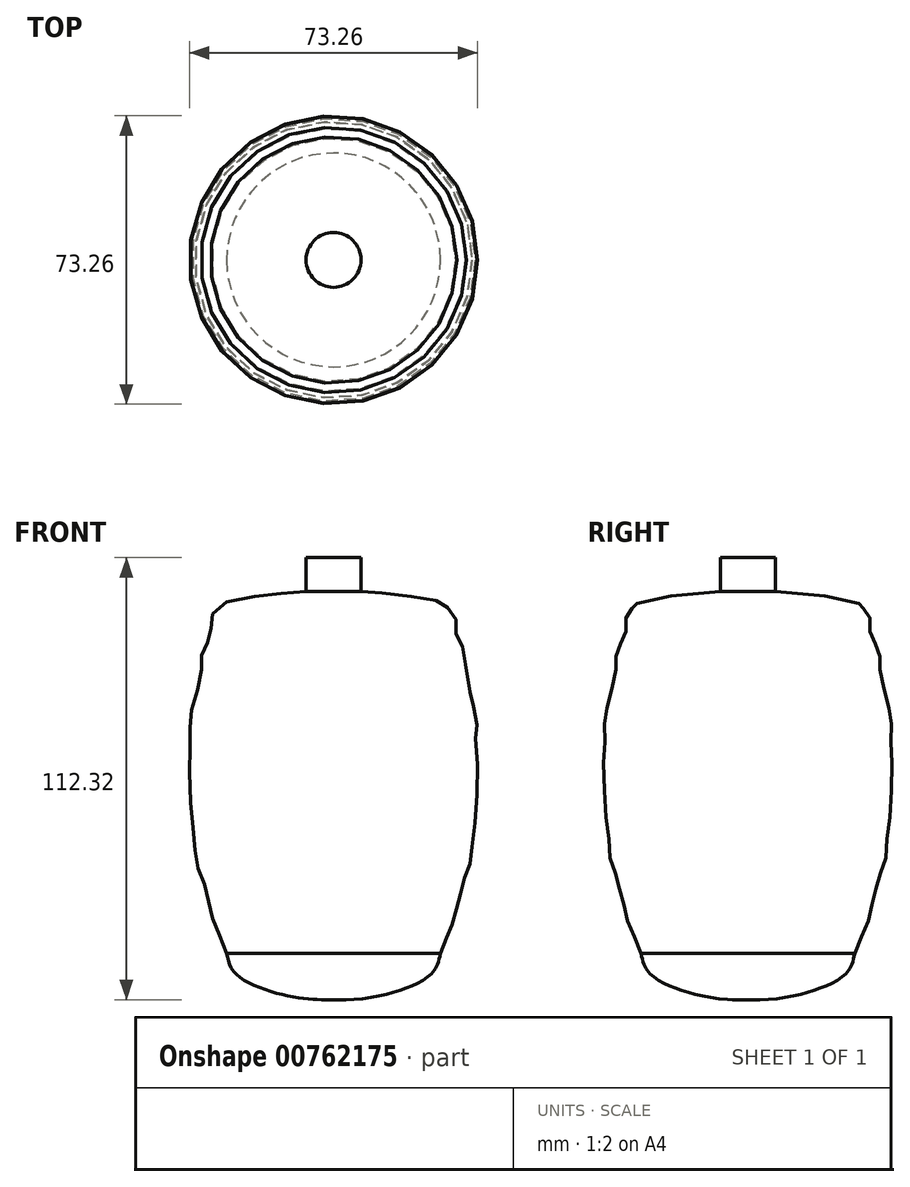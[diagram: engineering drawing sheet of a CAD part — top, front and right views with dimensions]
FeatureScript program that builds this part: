
annotation { "Feature Type Name" : "Feature", "Feature Type Description" : "" }
export const myFeature = defineFeature(function(context is Context, id is Id, definition is map)
    precondition{}
    {
        {
            var Q0;
            Q0=qCreatedBy(makeId("Front.planeOp"),FACE);
            var sketch = newSketch(context, id + "F0", { "sketchPlane" : qUnion([Q0])});
            skFitSpline(sketch, "E0", {"points": [v(-27.15, -40.38) * mm, v(-28.33, -37.93) * mm, v(-29.24, -34.76) * mm, v(-30, -33.44) * mm, v(-31.2, -29.96) * mm, v(-31.35, -28.56) * mm, v(-32.13, -25.81) * mm, v(-32.75, -23.24) * mm, v(-33.52, -20.4) * mm, v(-34.36, -18.84) * mm, v(-35.22, -14.06) * mm, v(-35.1, -13.17) * mm, v(-36.05, -6) * mm, v(-36.52, 2.74) * mm, v(-36.45, 12.07) * mm, v(-35.98, 15.83) * mm, v(-36.4, 17.1) * mm, v(-35.98, 21.55) * mm, v(-35.2, 22.77) * mm, v(-35.09, 23.87) * mm, v(-33.45, 32.8) * mm, v(-33.72, 33.54) * mm, v(-32.5, 38.07) * mm, v(-32.01, 38.55) * mm, v(-30.93, 41.64) * mm, v(-31.27, 42.43) * mm, v(-30.05, 46.96) * mm, v(-28.98, 47.38) * mm, v(-28.68, 48.01) * mm, v(-26.62, 49.07) * mm, v(-20.32, 50.23) * mm, v(-11.37, 51.2) * mm, v(-6.97, 51.53) * mm], "startDerivative": vector(-43.7, 75.94) * mm, "endDerivative": vector(105.8, 7.38) * mm});
            skLineSegment(sketch, "E1", {"start": v(-6.97, 51.53) * mm, "end": v(-6.97, 60.14) * mm});
            skLineSegment(sketch, "E2", {"start": v(-6.97, 60.14) * mm, "end": v(0, 60.14) * mm});
            skLineSegment(sketch, "E3", {"start": v(0, 60.14) * mm, "end": v(0, -52.09) * mm});
            skFitSpline(sketch, "E4", {"points": [v(0, -52.09) * mm, v(-5.65, -52.09) * mm, v(-15.96, -50.1) * mm, v(-25.15, -45.28) * mm, v(-27.15, -40.38) * mm], "startDerivative": vector(-24.58, -1.09) * mm, "endDerivative": vector(-5.1, 24.83) * mm});
            skSolve(sketch);
        }
        {
            var Q0;
            Q0 = qSketchRegion(id + "F0", true);
            var Q1;
            Q1=sQuery(id+"F0.wireOp",EDGE,"E3");
            revolve(context, id + "F1", {"surfaceOperationType" : NewSurfaceOperationType.NEW, "entities" : qUnion([Q0]), "axis" : qUnion([Q1]), "revolveType" : RevolveType.FULL});
        }
    });
